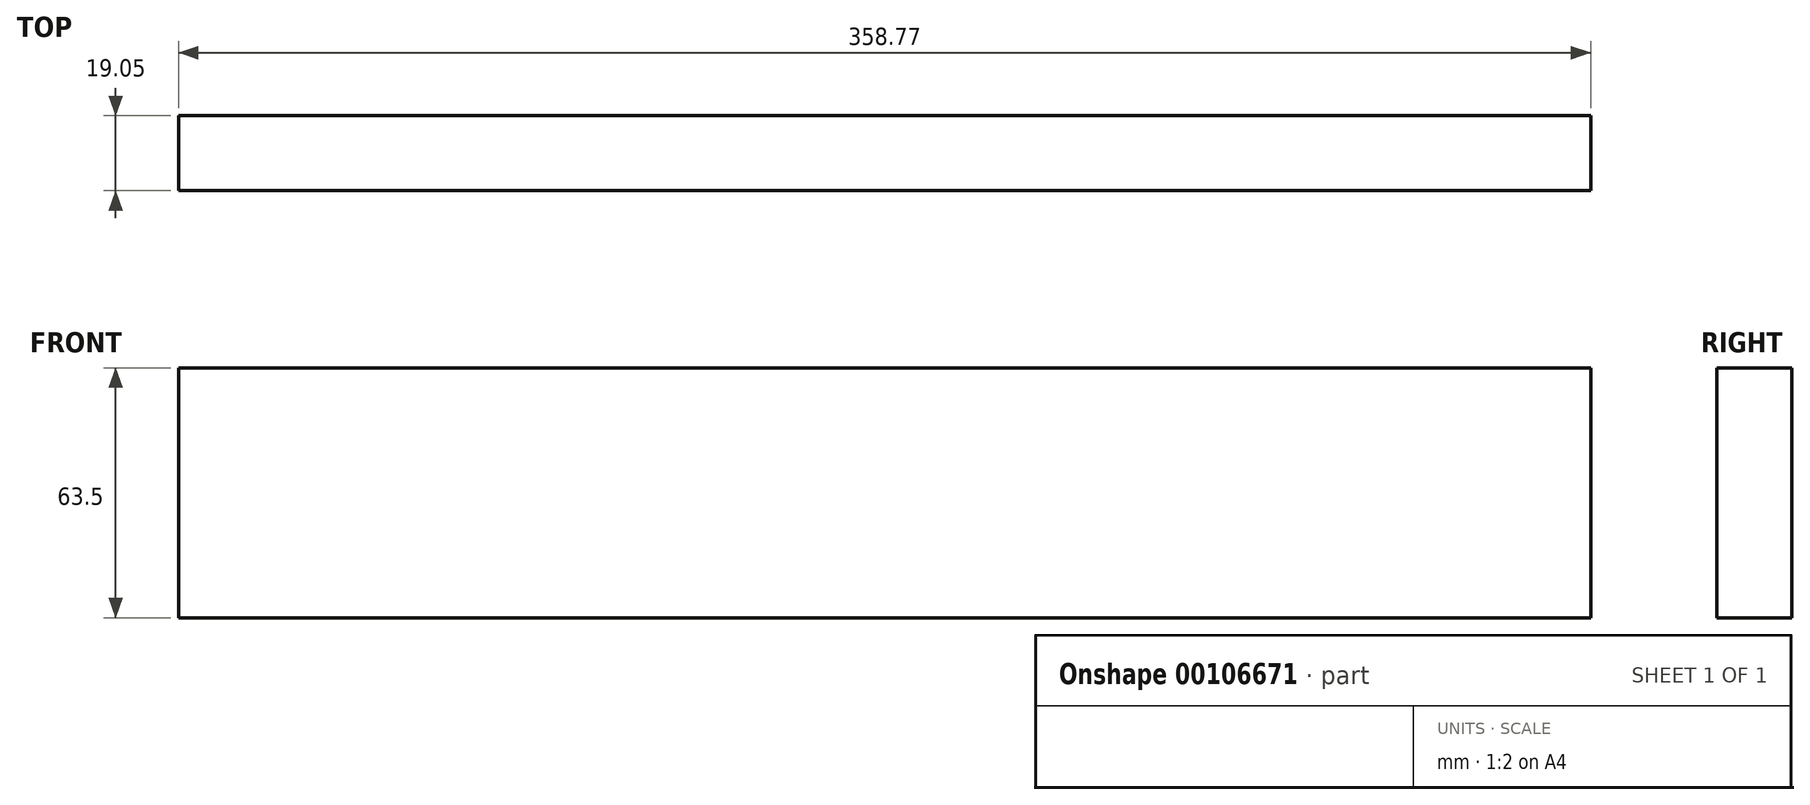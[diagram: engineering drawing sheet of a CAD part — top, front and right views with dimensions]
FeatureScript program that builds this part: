
annotation { "Feature Type Name" : "Feature", "Feature Type Description" : "" }
export const myFeature = defineFeature(function(context is Context, id is Id, definition is map)
    precondition{}
    {
        {
            var Q0;
            Q0=qCreatedBy(makeId("Front.planeOp"),FACE);
            var sketch = newSketch(context, id + "F0", { "sketchPlane" : qUnion([Q0])});
            skLineSegment(sketch, "E0.bottom", {"start": v(-149.6, -109.99) * mm, "end": v(209.18, -109.99) * mm});
            skLineSegment(sketch, "E0.top", {"start": v(-149.6, -46.49) * mm, "end": v(209.18, -46.49) * mm});
            skLineSegment(sketch, "E0.left", {"start": v(-149.6, -109.99) * mm, "end": v(-149.6, -46.49) * mm});
            skLineSegment(sketch, "E0.right", {"start": v(209.18, -109.99) * mm, "end": v(209.18, -46.49) * mm});
            skSolve(sketch);
        }
        {
            var Q0;
            Q0=makeQuery(id+"F0.imprint","IMPRINT",FACE,{"disambiguationData":[TD([[makeQuery(id+"F0.imprint","IMPRINT",EDGE,{"derivedFrom":sQuery(id+"F0.wireOp",EDGE,"E0.bottom")}),1.0]])]});
            extrude(context, id + "F1", {"entities" : qUnion([Q0]), "depth" : 19.05 * mm});
        }
    });
